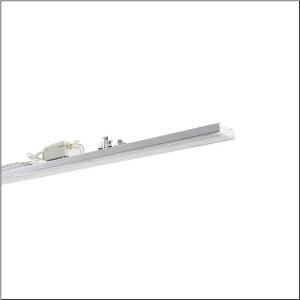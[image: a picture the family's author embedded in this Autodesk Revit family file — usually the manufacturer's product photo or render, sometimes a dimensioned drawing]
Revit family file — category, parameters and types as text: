
# Revit family: licross_r__21_recessed_mo_52te12cn49xg_2497
name_source: partatom
category: Lighting Fixtures
units: mm (PartAtom-declared; Revit-internal decimal feet)

## family parameters
Cut with Voids When Loaded = No
Host = Face
Light Source = No
Part Type = Normal
Room Calculation Point = No
Round Connector Dimension = Use Diameter
Shared = No

## types (1)
- --- (1 x LED, 9260 lm, 49.9 W, 4000K)
    Apparent Load = 50 VA
    CIE Flux Codes = 72 92 99 100 100
    Color Rendering = 80
    Color Temperature = 4000K
    Default Elevation = 1800 mm
    Description = Licross® 21 Recessed MO, luminaire insert, of sheet steel, galvanised, coil coated, white, length: 1.500mm, width: 66mm, height: 67mm, LED rated luminous flux: 9.260lm, light colour: 840, control gear: ON/OFF Multilumen, CLOi, control gear: ECG Multilumen, with plug, 3-pole, with phase selection, mains connection: 220..240V, AC, 50/60Hz, start of lifetime: 49W, end of service life: 61W, halogen-free wiring, primary optical cover: cover, of PMMA, light emission: direct distribution, primary light characteristic: symmetric, protection rating (complete): IP54, insulation class (complete): insulation class I (protective earthing), certification: CE, ENEC, VDE, UKCA, protection symbol: D if used in an environment with non-conductive dust loads with corresponding accessories, impact resistance: IK06, permissible ambient temperature for indoor applications: -35..+40°C, corresponds to IFS (International Featured Standards) requirements for safety and quality in the food industry, reducing of maximum allowable ambient temperature of 5°C with ceiling mounting, LABS conformity tested according to VDMA 24364:2018-05, packaging unit: 1 piece
    Height = 58 mm
    Lamp = 1 x LED
    Lamp Light Flux = 9260 lm
    Lamp Power = 49.9 W
    Lamp count = 1
    Length = 1500 mm
    Luminous efficacy = 186 lm/W
    Manufacturer = Siteco
    ModVariant = No
    Model = 52TE12CN49XG
    Mounting Place = Ceiling
    Mounting Type = Pendant
    Number of Poles = 1
    OnlyDefault = Yes
    Power Factor = 1
    Product Name = Licross® 21 Recessed MO
    Product group = luminaire insert
    ProductGroupID = 901
    Protection Class = Protection class I
    Protection Degree = IP 54
    RLX_Detail_Level = 1
    RLX_Emergency_Light_Flux = 0 lm
    RLX_Emergency_Type = 0
    RLX_Emergency_Type_DB = No
    RlxData = <blob elided: 22369 chars, md5=29d7c764>
    Socket = socket
    Standby Power = 0 W
    System Light Flux = 9260 lm
    System Power = 50 W
    Type Comments = factory setting: luminous flux: 100 % | (A | C | E) | 116 mA
    Type Image = l_1296930.jpg
    URL = http://relux.com
    VarID = @adj_079425
    Voltage = 0 V
    Weight = 0.00 kg
    Width = 66 mm

## geometry (parser evidence)
native form markers: Blend x4, Sweep x13
no freeform markers — native parametric forms only
